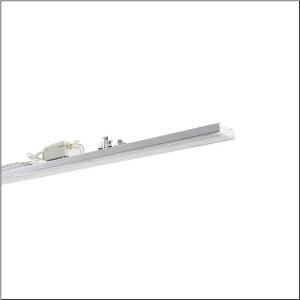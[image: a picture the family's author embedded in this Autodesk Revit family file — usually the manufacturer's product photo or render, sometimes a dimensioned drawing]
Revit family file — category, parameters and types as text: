
# Revit family: licross_r__21_recessed_mo_52tl18dn495g_5e12
name_source: partatom
category: Lighting Fixtures
units: mm (PartAtom-declared; Revit-internal decimal feet)

## family parameters
Cut with Voids When Loaded = No
Host = Face
Light Source = No
Part Type = Normal
Room Calculation Point = No
Round Connector Dimension = Use Diameter
Shared = No

## types (1)
- --- (1 x LED, 9990 lm, 58 W, 4000K)
    Apparent Load = 58 VA
    CIE Flux Codes = 79 95 99 100 100
    Color Rendering = 80
    Color Temperature = 4000K
    Default Elevation = 1800 mm
    Description = Licross® 21 Recessed MO, luminaire insert, of sheet steel, galvanised, coil coated, white, length: 1.500mm, width: 66mm, height: 67mm, LED rated luminous flux: 9.990lm, light colour: 840, control gear: DALI 2, with plug, 5-pole, with phase selection, mains connection: 220..240V, AC, 50/60Hz, rated input power: 58W, halogen-free wiring, primary light control with lens, of plastic, primary optical cover: cover, of PMMA, light emission: direct distribution, primary light characteristic: symmetric, protection rating (complete): IP40, insulation class (complete): insulation class I (protective earthing), certification: CE, ENEC, VDE, UKCA, protection symbol: D if used in an environment without relevant dust loads with corresponding accessories, impact resistance: IK06, permissible ambient temperature for indoor applications: -25..+35°C, corresponds to IFS (International Featured Standards) requirements for safety and quality in the food industry, reducing of maximum allowable ambient temperature of 5°C with ceiling mounting, LABS conformity tested according to VDMA 24364:2018-05, packaging unit: 1 piece
    Height = 58 mm
    Lamp = 1 x LED
    Lamp Light Flux = 9990 lm
    Lamp Power = 58 W
    Lamp count = 1
    Length = 1500 mm
    Luminous efficacy = 172 lm/W
    Manufacturer = Siteco
    ModVariant = No
    Model = 52TL18DN495G
    Mounting Place = Ceiling
    Mounting Type = Pendant
    Number of Poles = 1
    OnlyDefault = Yes
    Power Factor = 1
    Product Name = Licross® 21 Recessed MO
    Product group = luminaire insert
    ProductGroupID = 901
    Protection Class = Protection class I
    Protection Degree = IP 40
    RLX_Detail_Level = 1
    RLX_Emergency_Light_Flux = 0 lm
    RLX_Emergency_Type = 0
    RLX_Emergency_Type_DB = No
    RlxData = <blob elided: 24493 chars, md5=5a7d8986>
    Socket = socket
    Standby Power = 0 W
    System Light Flux = 9990 lm
    System Power = 58 W
    Type Comments = factory setting: luminous flux: 100 % | dim-lin: 254 | 390 mA
    Type Image = l_1296930.jpg
    URL = http://relux.com
    VarID = @adj_057501
    Voltage = 0 V
    Weight = 0.00 kg
    Width = 66 mm

## geometry (parser evidence)
native form markers: Blend x4, Sweep x12
no freeform markers — native parametric forms only
